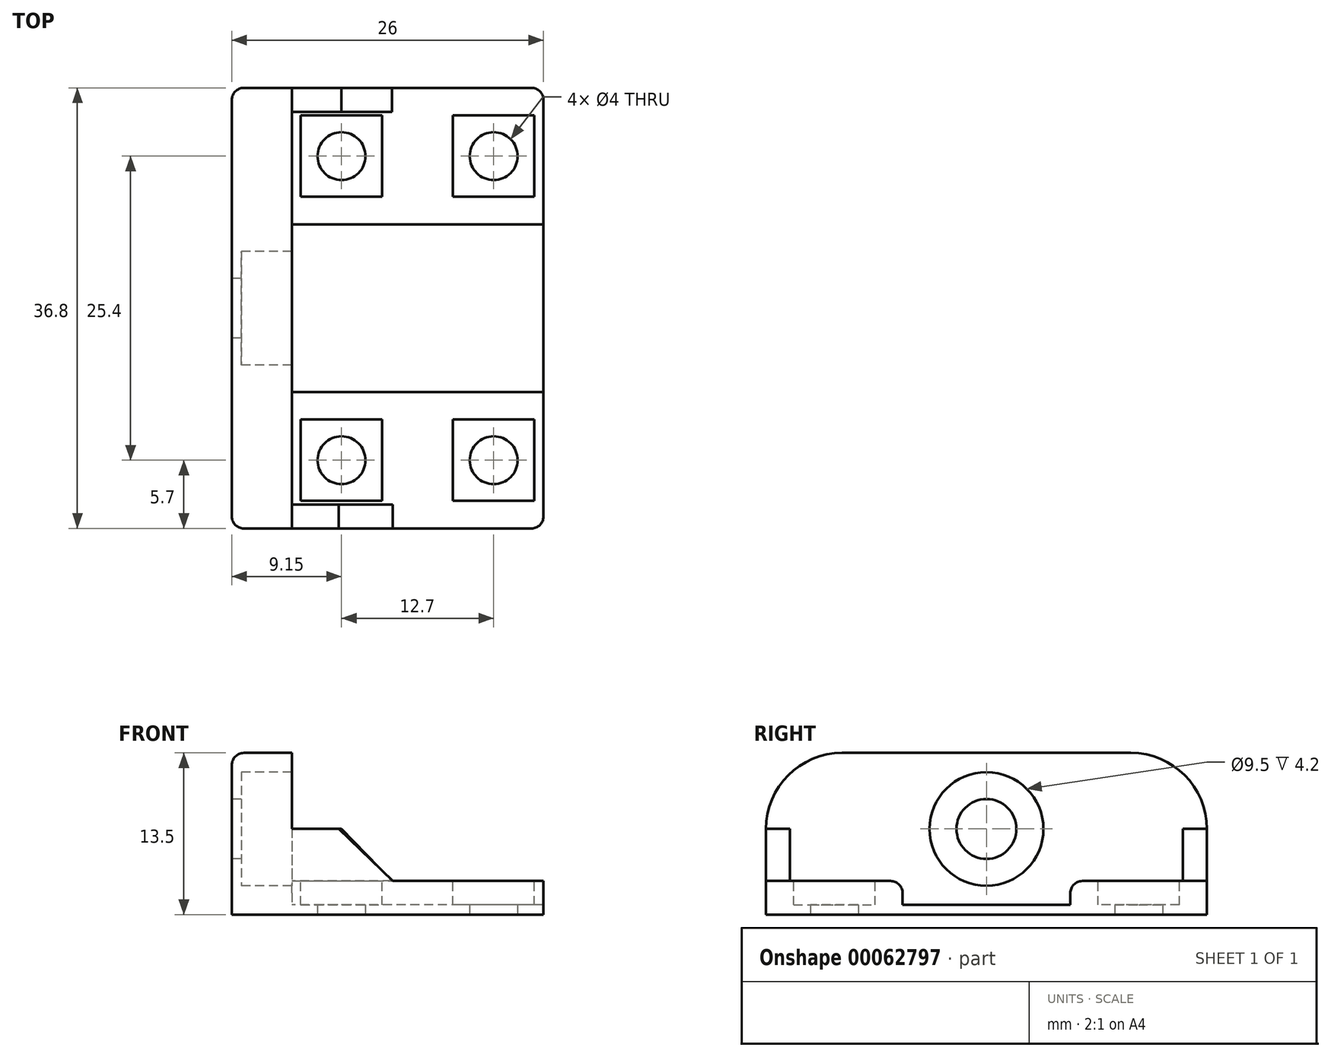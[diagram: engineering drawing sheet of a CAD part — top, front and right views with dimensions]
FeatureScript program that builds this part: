
annotation { "Feature Type Name" : "Feature", "Feature Type Description" : "" }
export const myFeature = defineFeature(function(context is Context, id is Id, definition is map)
    precondition{}
    {
        {
            var Q0;
            Q0=qCreatedBy(makeId("Top.planeOp"),FACE);
            var sketch = newSketch(context, id + "F0", { "sketchPlane" : qUnion([Q0])});
            skLineSegment(sketch, "E0.rect.bottom", {"start": v(10.5, 18.4) * mm, "end": v(-10.5, 18.4) * mm});
            skLineSegment(sketch, "E0.rect.top", {"start": v(10.5, -18.4) * mm, "end": v(-10.5, -18.4) * mm});
            skLineSegment(sketch, "E0.rect.left", {"start": v(10.5, 18.4) * mm, "end": v(10.5, -18.4) * mm});
            skLineSegment(sketch, "E0.rect.right", {"start": v(-10.5, 18.4) * mm, "end": v(-10.5, -18.4) * mm});
            skPoint(sketch, "E0.rect.middle", {"position": v(0, 0) * mm});
            skPoint(sketch, "E1", {"position": v(-6.35, -12.7) * mm});
            skCircle(sketch, "E2", {"center": v(-6.35, -12.7) * mm, "radius": 2 * mm});
            skCircle(sketch, "E3.0.1.0", {"center": v(-6.35, 12.7) * mm, "radius": 2 * mm});
            skCircle(sketch, "E3.1.0.0", {"center": v(6.35, -12.7) * mm, "radius": 2 * mm});
            skCircle(sketch, "E3.1.1.0", {"center": v(6.35, 12.7) * mm, "radius": 2 * mm});
            skLineSegment(sketch, "E3.direction1", {"start": v(-6.35, -12.7) * mm, "end": v(6.35, -12.7) * mm, "construction": true});
            skLineSegment(sketch, "E3.direction2", {"start": v(-6.35, -12.7) * mm, "end": v(-6.35, 12.7) * mm, "construction": true});
            skLineSegment(sketch, "E4.rect.bottom", {"start": v(-10.5, 18.4) * mm, "end": v(-15.5, 18.4) * mm});
            skLineSegment(sketch, "E4.rect.top", {"start": v(-10.5, -18.4) * mm, "end": v(-15.5, -18.4) * mm});
            skLineSegment(sketch, "E4.rect.right", {"start": v(-15.5, 18.4) * mm, "end": v(-15.5, -18.4) * mm});
            skPoint(sketch, "E4.rect.middle", {"position": v(-13, 0) * mm});
            skSolve(sketch);
        }
        {
            var Q0;
            {var subQ0=sQuery(id+"F0.wireOp",EDGE,"E0.rect.bottom");Q0=makeQuery(id+"F0.imprint","IMPRINT",FACE,{"disambiguationData":[TD([[makeQuery(id+"F0.imprint","IMPRINT",EDGE,{"derivedFrom":subQ0}),1.0]])]});}
            extrude(context, id + "F1", {"entities" : qUnion([Q0]), "depth" : 0.8 * mm});
        }
        {
            var Q0;
            Q0=makeQuery(id+"F0.imprint","IMPRINT",FACE,{"disambiguationData":[TD([[makeQuery(id+"F0.imprint","IMPRINT",EDGE,{"derivedFrom":sQuery(id+"F0.wireOp",EDGE,"E4.rect.bottom")}),1.0]])]});
            extrude(context, id + "F2", {"entities" : qUnion([Q0]), "operationType" : NewBodyOperationType.ADD, "depth" : 13.5 * mm});
        }
        {
            var Q0;
            Q0=makeQuery(id+"F1.opExtrude","CAP_FACE",FACE,{"disambiguationData":[OSD([sQuery(id+"F0.wireOp",EDGE,"E0.rect.bottom"),sQuery(id+"F0.wireOp",EDGE,"E0.rect.top"),sQuery(id+"F0.wireOp",EDGE,"E0.rect.left"),sQuery(id+"F0.wireOp",EDGE,"E0.rect.right"),sQuery(id+"F0.wireOp",EDGE,"E2"),sQuery(id+"F0.wireOp",EDGE,"E3.0.1.0"),sQuery(id+"F0.wireOp",EDGE,"E3.0.2.0"),sQuery(id+"F0.wireOp",EDGE,"E3.1.0.0"),sQuery(id+"F0.wireOp",EDGE,"E3.1.1.0"),sQuery(id+"F0.wireOp",EDGE,"E3.1.2.0"),sQuery(id+"F0.wireOp",EDGE,"E4.rect.bottom"),sQuery(id+"F0.wireOp",EDGE,"E4.rect.top"),sQuery(id+"F0.wireOp",EDGE,"E4.rect.right"),sQuery(id+"F0.wireOp",EDGE,"b8cd94a5-6213-4f24-92a0-501cbafc5d1e0.MirrorCS"),sQuery(id+"F0.wireOp",EDGE,"5aaf3535-5eb7-4c54-adac-0a11be8deb510.MirrorCS"),sQuery(id+"F0.wireOp",EDGE,"d065ad54-db49-492f-a6e4-d5afd2cb632a0.MirrorCS")])],"isStart":false});
            var sketch = newSketch(context, id + "F3", { "sketchPlane" : qUnion([Q0])});
            skLineSegment(sketch, "E5", {"start": v(-10.5, 18.4) * mm, "end": v(-10.5, -18.4) * mm});
            skLineSegment(sketch, "E6", {"start": v(10.5, 18.4) * mm, "end": v(10.5, 18.4) * mm});
            skSolve(sketch);
        }
        {
            var Q0;
            Q0=makeQuery(id+"F2.opExtrude","SWEPT_FACE",FACE,{"disambiguationData":[OSD([sQuery(id+"F0.wireOp",EDGE,"E0.rect.right")])]});
            var sketch = newSketch(context, id + "F4", { "sketchPlane" : qUnion([Q0])});
            skPoint(sketch, "E7", {"position": v(0, 7.15) * mm});
            skSolve(sketch);
        }
        {
            var Q0;
            Q0=makeQuery(id+"F2.opExtrude","CAP_EDGE",EDGE,{"disambiguationData":[OSD([sQuery(id+"F0.wireOp",EDGE,"E4.rect.top")])],"isStart":false});
            var Q1;
            Q1=makeQuery(id+"F2.opExtrude","CAP_EDGE",EDGE,{"disambiguationData":[OSD([sQuery(id+"F0.wireOp",EDGE,"E4.rect.bottom")])],"isStart":false});
            fillet(context, id + "F5", {"entities" : qUnion([Q0, Q1]), "radius" : 6.35 * mm, "tangentPropagation" : true, "allowEdgeOverflow" : false});
        }
        {
            var Q0;
            Q0=sQuery(id+"F4.wireOp",VERTEX,"E7");
            var Q1;
            Q1=makeQuery(id+"F1.opExtrude","SWEPT_BODY",BODY,{"disambiguationData":[OSD([sQuery(id+"F0.wireOp",EDGE,"E0.rect.bottom"),sQuery(id+"F0.wireOp",EDGE,"E0.rect.top"),sQuery(id+"F0.wireOp",EDGE,"E0.rect.left"),sQuery(id+"F0.wireOp",EDGE,"E0.rect.right"),sQuery(id+"F0.wireOp",EDGE,"E2"),sQuery(id+"F0.wireOp",EDGE,"E3.0.1.0"),sQuery(id+"F0.wireOp",EDGE,"E3.0.2.0"),sQuery(id+"F0.wireOp",EDGE,"E3.1.0.0"),sQuery(id+"F0.wireOp",EDGE,"E3.1.1.0"),sQuery(id+"F0.wireOp",EDGE,"E3.1.2.0"),sQuery(id+"F0.wireOp",EDGE,"E4.rect.bottom"),sQuery(id+"F0.wireOp",EDGE,"E4.rect.top"),sQuery(id+"F0.wireOp",EDGE,"E4.rect.right"),sQuery(id+"F0.wireOp",EDGE,"b8cd94a5-6213-4f24-92a0-501cbafc5d1e0.MirrorCS"),sQuery(id+"F0.wireOp",EDGE,"5aaf3535-5eb7-4c54-adac-0a11be8deb510.MirrorCS"),sQuery(id+"F0.wireOp",EDGE,"d065ad54-db49-492f-a6e4-d5afd2cb632a0.MirrorCS")])]});
            hole(context, id + "F6", {"style" : HoleStyle.C_BORE, "holeDiameter" : 5 * mm, "cBoreDiameter" : 9.5 * mm, "cBoreDepth" : 4.2 * mm, "endStyle" : HoleEndStyle.THROUGH, "locations" : qUnion([Q0]), "scope" : qUnion([Q1]), "isTappedThrough" : true});
        }
        {
            var Q0;
            Q0=makeQuery(id+"F3.imprint","IMPRINT",FACE,{"disambiguationData":[TD([[makeQuery(id+"F3.imprint","IMPRINT",EDGE,{"derivedFrom":sQuery(id+"F3.wireOp",EDGE,"E5")}),1.0]])]});
            var sketch = newSketch(context, id + "F7", { "sketchPlane" : qUnion([Q0])});
            skLineSegment(sketch, "E8.bottom", {"start": v(0, -16.4) * mm, "end": v(-10.5, -16.4) * mm});
            skLineSegment(sketch, "E8.top", {"start": v(0, -18.4) * mm, "end": v(-10.5, -18.4) * mm});
            skLineSegment(sketch, "E8.left", {"start": v(0, -16.4) * mm, "end": v(0, -18.4) * mm});
            skLineSegment(sketch, "E8.right", {"start": v(-10.5, -16.4) * mm, "end": v(-10.5, -18.4) * mm});
            skLineSegment(sketch, "E9.bottom", {"start": v(10.5, -18.4) * mm, "end": v(-10.5, -18.4) * mm});
            skLineSegment(sketch, "E9.top", {"start": v(10.5, -7) * mm, "end": v(-10.5, -7) * mm});
            skLineSegment(sketch, "E9.left", {"start": v(10.5, -18.4) * mm, "end": v(10.5, -7) * mm});
            skLineSegment(sketch, "E9.right", {"start": v(-10.5, -18.4) * mm, "end": v(-10.5, -7) * mm});
            skPoint(sketch, "E9.middle", {"position": v(0, -12.7) * mm});
            skLineSegment(sketch, "E10.MirrorCS", {"start": v(10.5, 7) * mm, "end": v(-10.5, 7) * mm});
            skLineSegment(sketch, "E11.MirrorCS", {"start": v(0, 16.4) * mm, "end": v(0, 18.4) * mm});
            skLineSegment(sketch, "E12.MirrorCS", {"start": v(0, 16.4) * mm, "end": v(-10.5, 16.4) * mm});
            skSolve(sketch);
        }
        {
            var Q0;
            Q0 = qSketchRegion(id + "F7", true);
            var Q1;
            {var subQ2=sQuery(id+"F7.wireOp",EDGE,"E10.MirrorCS");Q1=makeQuery(id+"F7.imprint","IMPRINT",FACE,{"disambiguationData":[TD([[makeQuery(id+"F7.imprint","IMPRINT",EDGE,{"derivedFrom":subQ2}),-1.0]])]});}
            extrude(context, id + "F8", {"entities" : qUnion([Q0, Q1]), "operationType" : NewBodyOperationType.ADD, "depth" : 2 * mm});
        }
        {
            var Q0;
            Q0=makeQuery(id+"F7.imprint","IMPRINT",FACE,{"disambiguationData":[TD([[makeQuery(id+"F7.imprint","IMPRINT",EDGE,{"derivedFrom":sQuery(id+"F7.wireOp",EDGE,"E8.bottom")}),1.0]])]});
            var Q1;
            {var subQ0=sQuery(id+"F7.wireOp",EDGE,"E11.MirrorCS");Q1=makeQuery(id+"F7.imprint","IMPRINT",FACE,{"disambiguationData":[TD([[makeQuery(id+"F7.imprint","IMPRINT",EDGE,{"derivedFrom":subQ0}),1.0]])]});}
            extrude(context, id + "F9", {"entities" : qUnion([Q0, Q1]), "operationType" : NewBodyOperationType.ADD, "depth" : 6.35 * mm});
        }
        {
            var Q0;
            Q0=makeQuery(id+"F9.opExtrude","CAP_EDGE",EDGE,{"disambiguationData":[OSD([sQuery(id+"F7.wireOp",EDGE,"E8.left")])],"isStart":false});
            var Q1;
            Q1=makeQuery(id+"F9.opExtrude","CAP_EDGE",EDGE,{"disambiguationData":[OSD([sQuery(id+"F7.wireOp",EDGE,"E11.MirrorCS")])],"isStart":false});
            chamfer(context, id + "F10", {"entities" : qUnion([Q0, Q1]), "chamferType" : ChamferType.OFFSET_ANGLE, "width" : 6.35 * mm, "oppositeDirection" : false, "angle" : 46 * degree, "tangentPropagation" : true});
        }
        {
            var Q0;
            Q0=makeQuery(id+"F8.opExtrude","CAP_FACE",FACE,{"disambiguationData":[OSD([sQuery(id+"F7.wireOp",EDGE,"E9.bottom"),sQuery(id+"F7.wireOp",EDGE,"E9.top"),sQuery(id+"F7.wireOp",EDGE,"E9.left"),sQuery(id+"F7.wireOp",EDGE,"E9.right")])],"isStart":false});
            var sketch = newSketch(context, id + "F11", { "sketchPlane" : qUnion([Q0])});
            skPoint(sketch, "E13", {"position": v(6.35, -12.7) * mm});
            skPoint(sketch, "E14.MirrorP", {"position": v(-6.35, -12.7) * mm});
            skLineSegment(sketch, "E15.bottom", {"start": v(9.75, -16.1) * mm, "end": v(2.95, -16.1) * mm});
            skLineSegment(sketch, "E15.top", {"start": v(9.75, -9.3) * mm, "end": v(2.95, -9.3) * mm});
            skLineSegment(sketch, "E15.left", {"start": v(9.75, -16.1) * mm, "end": v(9.75, -9.3) * mm});
            skLineSegment(sketch, "E15.right", {"start": v(2.95, -16.1) * mm, "end": v(2.95, -9.3) * mm});
            skLineSegment(sketch, "E16.MirrorCS", {"start": v(-2.95, -16.1) * mm, "end": v(-2.95, -9.3) * mm});
            skLineSegment(sketch, "E17.MirrorCS", {"start": v(-9.75, -9.3) * mm, "end": v(-2.95, -9.3) * mm});
            skLineSegment(sketch, "E18.MirrorCS", {"start": v(-9.75, -16.1) * mm, "end": v(-9.75, -9.3) * mm});
            skLineSegment(sketch, "E19.MirrorCS", {"start": v(-9.75, -16.1) * mm, "end": v(-2.95, -16.1) * mm});
            skLineSegment(sketch, "E20.MirrorCS", {"start": v(-9.75, 9.3) * mm, "end": v(-2.95, 9.3) * mm});
            skLineSegment(sketch, "E21.MirrorCS", {"start": v(-9.75, 16.1) * mm, "end": v(-9.75, 9.3) * mm});
            skLineSegment(sketch, "E22.MirrorCS", {"start": v(-9.75, 16.1) * mm, "end": v(-2.95, 16.1) * mm});
            skLineSegment(sketch, "E23.MirrorCS", {"start": v(-2.95, 16.1) * mm, "end": v(-2.95, 9.3) * mm});
            skLineSegment(sketch, "E24.MirrorCS", {"start": v(2.95, 16.1) * mm, "end": v(2.95, 9.3) * mm});
            skLineSegment(sketch, "E25.MirrorCS", {"start": v(9.75, 16.1) * mm, "end": v(2.95, 16.1) * mm});
            skLineSegment(sketch, "E26.MirrorCS", {"start": v(9.75, 16.1) * mm, "end": v(9.75, 9.3) * mm});
            skLineSegment(sketch, "E27.MirrorCS", {"start": v(9.75, 9.3) * mm, "end": v(2.95, 9.3) * mm});
            skSolve(sketch);
        }
        {
            var Q0;
            Q0=makeQuery(id+"F11.imprint","IMPRINT",FACE,{"disambiguationData":[TD([[makeQuery(id+"F11.imprint","IMPRINT",EDGE,{"derivedFrom":sQuery(id+"F11.wireOp",EDGE,"E16.MirrorCS")}),1.0]])]});
            var Q1;
            Q1=makeQuery(id+"F11.imprint","IMPRINT",FACE,{"disambiguationData":[TD([[makeQuery(id+"F11.imprint","IMPRINT",EDGE,{"derivedFrom":sQuery(id+"F11.wireOp",EDGE,"E15.bottom")}),-1.0]])]});
            var Q2;
            Q2=makeQuery(id+"F11.imprint","IMPRINT",FACE,{"disambiguationData":[TD([[makeQuery(id+"F11.imprint","IMPRINT",EDGE,{"derivedFrom":sQuery(id+"F11.wireOp",EDGE,"E20.MirrorCS")}),1.0]])]});
            var Q3;
            Q3=makeQuery(id+"F11.imprint","IMPRINT",FACE,{"disambiguationData":[TD([[makeQuery(id+"F11.imprint","IMPRINT",EDGE,{"derivedFrom":sQuery(id+"F11.wireOp",EDGE,"E24.MirrorCS")}),1.0]])]});
            extrude(context, id + "F12", {"entities" : qUnion([Q0, Q1, Q2, Q3]), "operationType" : NewBodyOperationType.REMOVE, "oppositeDirection" : true, "depth" : 2 * mm});
        }
        {
            var Q0;
            Q0=makeQuery(id+"F8.boolean.opBoolean","MERGE",EDGE,{"derivedFrom":[makeQuery(id+"F1.opExtrude","SWEPT_EDGE",EDGE,{"disambiguationData":[OSD([sQuery(id+"F0.wireOp",EDGE,"E0.rect.top"),sQuery(id+"F0.wireOp",EDGE,"E0.rect.left")])]}),makeQuery(id+"F8.opExtrude","SWEPT_EDGE",EDGE,{"disambiguationData":[OSD([sQuery(id+"F7.wireOp",EDGE,"E9.bottom"),sQuery(id+"F7.wireOp",EDGE,"E9.left")])]})]});
            var Q1;
            {var subQ0=sQuery(id+"F0.wireOp",EDGE,"E0.rect.left");var subQ1=sQuery(id+"F0.wireOp",EDGE,"E0.rect.bottom");Q1=makeQuery(id+"F8.boolean.opBoolean","MERGE",EDGE,{"derivedFrom":[makeQuery(id+"F1.opExtrude","SWEPT_EDGE",EDGE,{"disambiguationData":[OSD([subQ1,subQ0])]}),makeQuery(id+"F8.opExtrude","SWEPT_EDGE",EDGE,{"disambiguationData":[OSD([subQ1,subQ0])]})]});}
            var Q2;
            Q2=makeQuery(id+"F2.opExtrude","SWEPT_EDGE",EDGE,{"disambiguationData":[OSD([sQuery(id+"F0.wireOp",EDGE,"E4.rect.top"),sQuery(id+"F0.wireOp",EDGE,"E4.rect.right")])]});
            var Q3;
            Q3=makeQuery(id+"F8.opExtrude","CAP_EDGE",EDGE,{"disambiguationData":[OSD([sQuery(id+"F7.wireOp",EDGE,"E10.MirrorCS")])],"isStart":true});
            var Q4;
            Q4=makeQuery(id+"F8.opExtrude","CAP_EDGE",EDGE,{"disambiguationData":[OSD([sQuery(id+"F7.wireOp",EDGE,"E9.top")])],"isStart":true});
            var Q5;
            Q5=makeQuery(id+"F8.opExtrude","CAP_EDGE",EDGE,{"disambiguationData":[OSD([sQuery(id+"F7.wireOp",EDGE,"E10.MirrorCS")])],"isStart":false});
            var Q6;
            Q6=makeQuery(id+"F8.opExtrude","CAP_EDGE",EDGE,{"disambiguationData":[OSD([sQuery(id+"F7.wireOp",EDGE,"E9.top")])],"isStart":false});
            fillet(context, id + "F13", {"entities" : qUnion([Q0, Q1, Q2, Q3, Q4, Q5, Q6]), "radius" : 1 * mm, "tangentPropagation" : true, "allowEdgeOverflow" : false});
        }
    });
